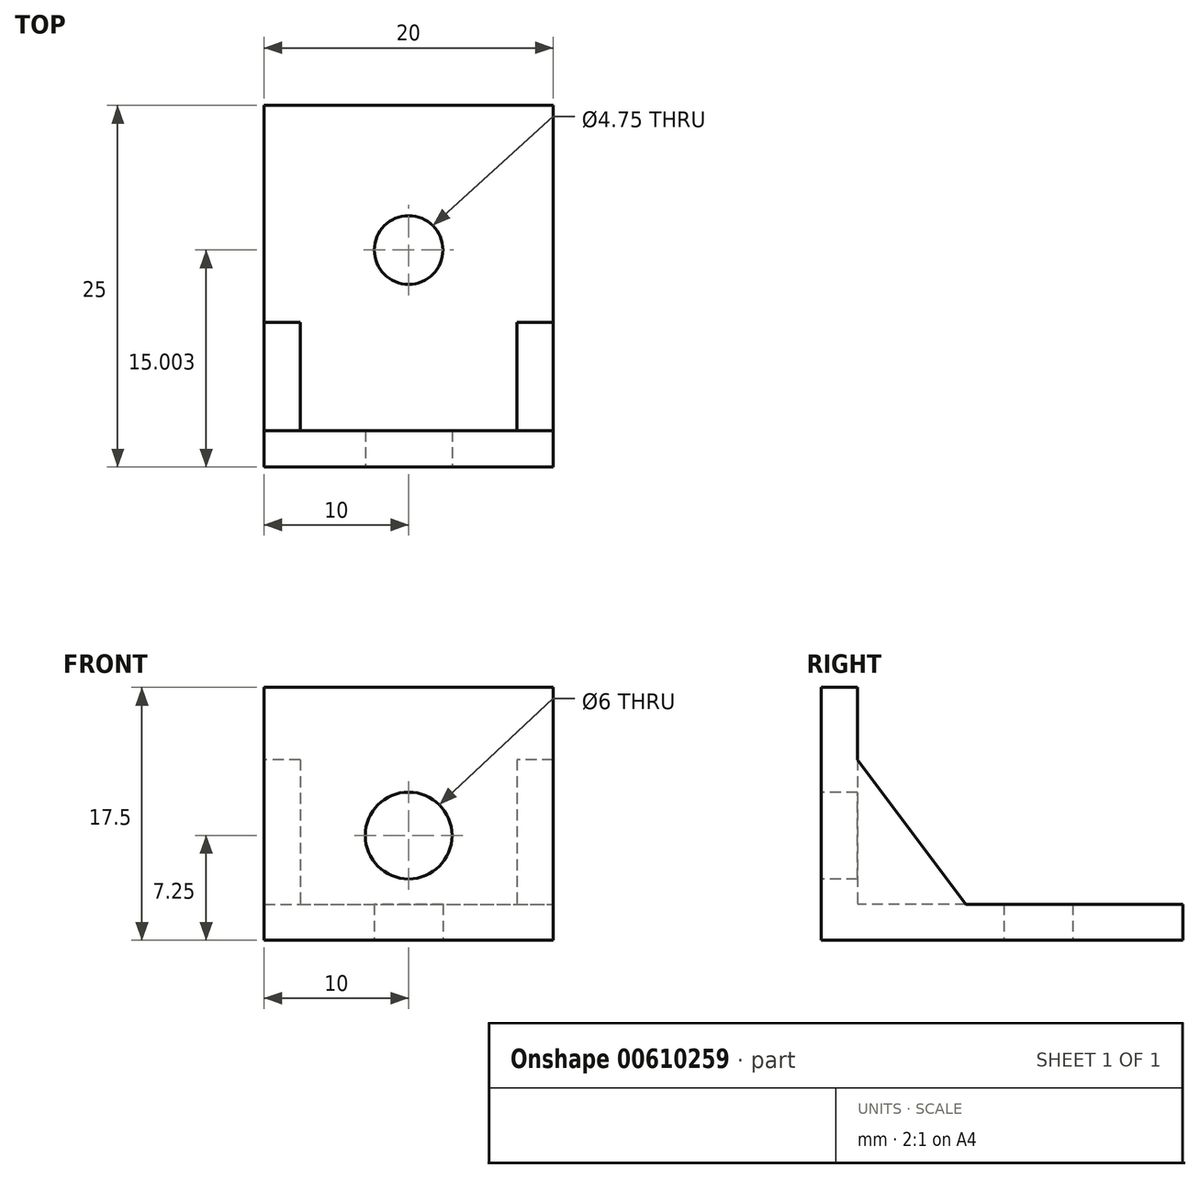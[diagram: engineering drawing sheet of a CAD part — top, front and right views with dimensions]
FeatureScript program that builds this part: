
annotation { "Feature Type Name" : "Feature", "Feature Type Description" : "" }
export const myFeature = defineFeature(function(context is Context, id is Id, definition is map)
    precondition{}
    {
        {
            var Q0;
            Q0=qCreatedBy(makeId("Top.planeOp"),FACE);
            var sketch = newSketch(context, id + "F0", { "sketchPlane" : qUnion([Q0])});
            skLineSegment(sketch, "E0.bottom", {"start": v(-45.04, -13.09) * mm, "end": v(-25.04, -13.09) * mm});
            skLineSegment(sketch, "E0.top", {"start": v(-45.04, -38.09) * mm, "end": v(-25.04, -38.09) * mm});
            skLineSegment(sketch, "E0.left", {"start": v(-45.04, -13.09) * mm, "end": v(-45.04, -38.09) * mm});
            skLineSegment(sketch, "E0.right", {"start": v(-25.04, -13.09) * mm, "end": v(-25.04, -38.09) * mm});
            skCircle(sketch, "E1", {"center": v(-35.04, -23.09) * mm, "radius": 2.38 * mm});
            skSolve(sketch);
        }
        {
            var Q0;
            Q0=makeQuery(id+"F0.imprint","IMPRINT",FACE,{"disambiguationData":[TD([[makeQuery(id+"F0.imprint","IMPRINT",EDGE,{"derivedFrom":sQuery(id+"F0.wireOp",EDGE,"E0.bottom")}),-1.0]])]});
            extrude(context, id + "F1", {"entities" : qUnion([Q0]), "depth" : 2.5 * mm, "offsetDistance" : 25.4 * mm});
        }
        {
            var Q0;
            Q0=makeQuery(id+"F1.opExtrude","CAP_FACE",FACE,{"disambiguationData":[OSD([sQuery(id+"F0.wireOp",EDGE,"E0.bottom"),sQuery(id+"F0.wireOp",EDGE,"E0.top"),sQuery(id+"F0.wireOp",EDGE,"E0.left"),sQuery(id+"F0.wireOp",EDGE,"E0.right"),sQuery(id+"F0.wireOp",EDGE,"E1")])],"isStart":false});
            var sketch = newSketch(context, id + "F2", { "sketchPlane" : qUnion([Q0])});
            skLineSegment(sketch, "E2", {"start": v(-45.04, -28.09) * mm, "end": v(-42.54, -28.09) * mm});
            skLineSegment(sketch, "E3", {"start": v(-42.54, -28.09) * mm, "end": v(-42.54, -35.59) * mm});
            skLineSegment(sketch, "E4", {"start": v(-42.54, -35.59) * mm, "end": v(-27.54, -35.59) * mm});
            skLineSegment(sketch, "E5", {"start": v(-27.54, -35.59) * mm, "end": v(-27.54, -28.09) * mm});
            skLineSegment(sketch, "E6", {"start": v(-27.54, -28.09) * mm, "end": v(-25.04, -28.09) * mm});
            skLineSegment(sketch, "E7", {"start": v(-25.04, -28.09) * mm, "end": v(-25.04, -38.09) * mm});
            skLineSegment(sketch, "E8", {"start": v(-25.04, -38.09) * mm, "end": v(-45.04, -38.09) * mm});
            skLineSegment(sketch, "E9", {"start": v(-45.04, -38.09) * mm, "end": v(-45.04, -28.09) * mm});
            skSolve(sketch);
        }
        {
            var Q0;
            Q0=makeQuery(id+"F2.imprint","IMPRINT",FACE,{"disambiguationData":[TD([[makeQuery(id+"F2.imprint","IMPRINT",EDGE,{"derivedFrom":sQuery(id+"F2.wireOp",EDGE,"E2")}),-1.0]])]});
            extrude(context, id + "F3", {"entities" : qUnion([Q0]), "operationType" : NewBodyOperationType.ADD, "depth" : 10 * mm, "offsetDistance" : 25.4 * mm});
        }
        {
            var Q0;
            Q0=makeQuery(id+"F3.opExtrude","CAP_EDGE",EDGE,{"disambiguationData":[OSD([sQuery(id+"F2.wireOp",EDGE,"E2")])],"isStart":false});
            var Q1;
            Q1=makeQuery(id+"F3.opExtrude","CAP_EDGE",EDGE,{"disambiguationData":[OSD([sQuery(id+"F2.wireOp",EDGE,"E6")])],"isStart":false});
            chamfer(context, id + "F4", {"entities" : qUnion([Q0, Q1]), "chamferType" : ChamferType.TWO_OFFSETS, "width1" : 10 * mm, "oppositeDirection" : false, "width2" : 7.5 * mm, "tangentPropagation" : true});
        }
        {
            var Q0;
            Q0=makeQuery(id+"F3.opExtrude","CAP_FACE",FACE,{"disambiguationData":[OSD([sQuery(id+"F2.wireOp",EDGE,"E2"),sQuery(id+"F2.wireOp",EDGE,"E3"),sQuery(id+"F2.wireOp",EDGE,"E4"),sQuery(id+"F2.wireOp",EDGE,"E5"),sQuery(id+"F2.wireOp",EDGE,"E6"),sQuery(id+"F2.wireOp",EDGE,"E7"),sQuery(id+"F2.wireOp",EDGE,"E8"),sQuery(id+"F2.wireOp",EDGE,"E9")])],"isStart":false});
            extrude(context, id + "F5", {"entities" : qUnion([Q0]), "operationType" : NewBodyOperationType.ADD, "depth" : 5 * mm, "offsetDistance" : 25.4 * mm});
        }
        {
            var Q0;
            {var subQ0=sQuery(id+"F2.wireOp",EDGE,"E8");Q0=makeQuery(id+"F5.boolean.opBoolean","MERGE",FACE,{"derivedFrom":[makeQuery(id+"F3.boolean.opBoolean","MERGE",FACE,{"derivedFrom":[makeQuery(id+"F1.opExtrude","SWEPT_FACE",FACE,{"disambiguationData":[OSD([sQuery(id+"F0.wireOp",EDGE,"E0.top")])]}),makeQuery(id+"F3.opExtrude","SWEPT_FACE",FACE,{"disambiguationData":[OSD([subQ0])]})]}),makeQuery(id+"F5.opExtrude","SWEPT_FACE",FACE,{"disambiguationData":[OSD([subQ0])]})]});}
            var sketch = newSketch(context, id + "F6", { "sketchPlane" : qUnion([Q0])});
            skCircle(sketch, "E10", {"center": v(-35.04, 7.25) * mm, "radius": 3 * mm});
            skSolve(sketch);
        }
        {
            var Q0;
            Q0=makeQuery(id+"F6.imprint","IMPRINT",FACE,{"disambiguationData":[TD([[makeQuery(id+"F6.imprint","IMPRINT",EDGE,{"derivedFrom":sQuery(id+"F6.wireOp",EDGE,"E10")}),1.0]])]});
            extrude(context, id + "F7", {"entities" : qUnion([Q0]), "operationType" : NewBodyOperationType.REMOVE, "oppositeDirection" : true, "depth" : 2.5 * mm, "offsetDistance" : 25.4 * mm});
        }
    });
